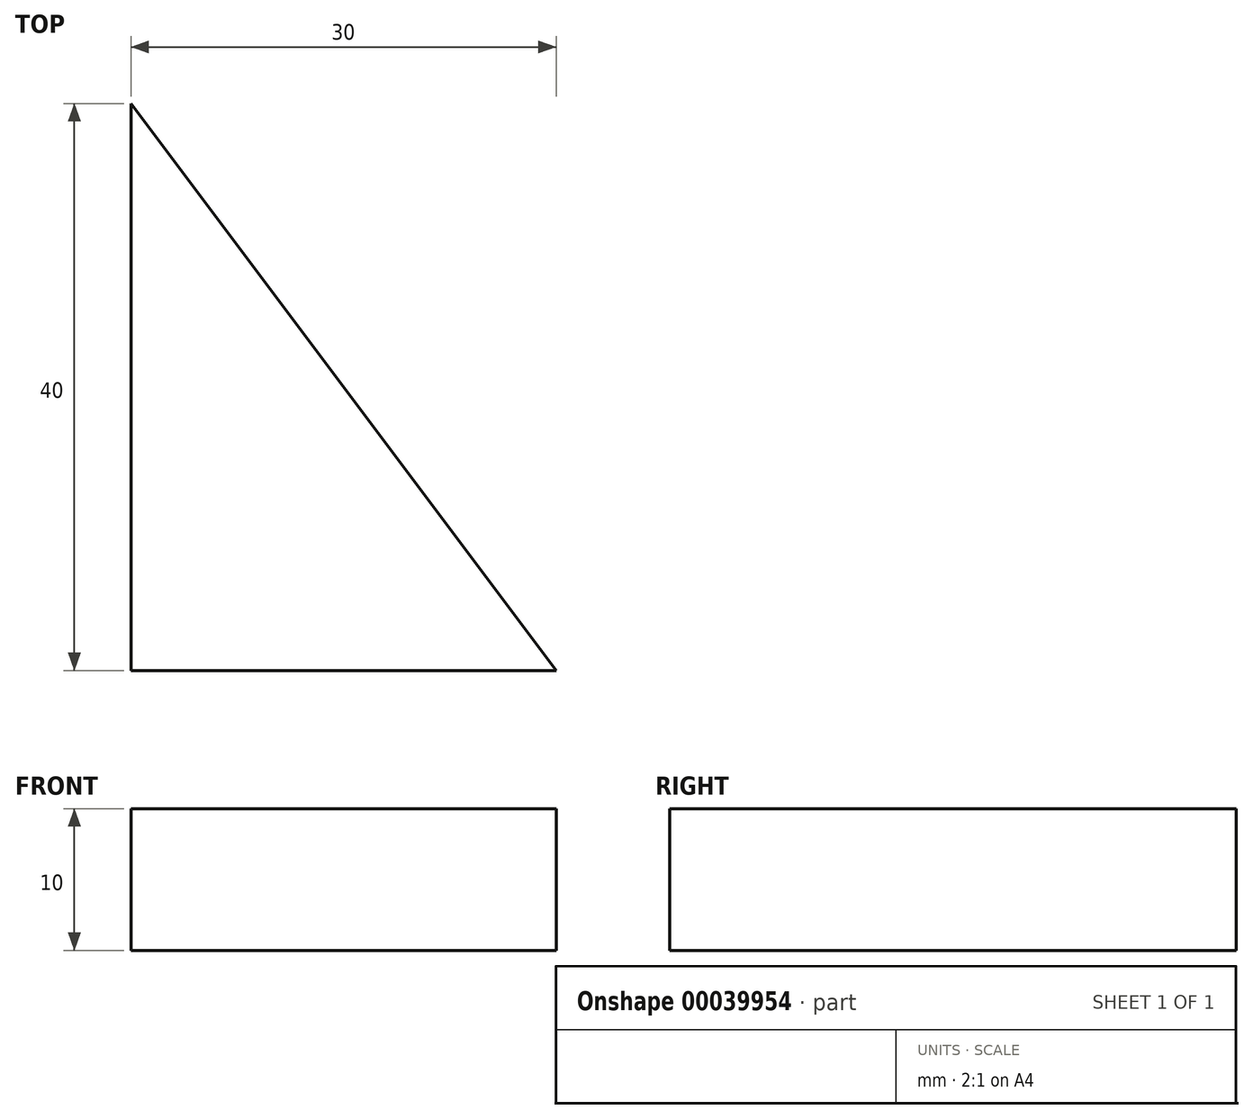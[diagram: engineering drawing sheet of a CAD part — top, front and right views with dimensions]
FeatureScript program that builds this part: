
annotation { "Feature Type Name" : "Feature", "Feature Type Description" : "" }
export const myFeature = defineFeature(function(context is Context, id is Id, definition is map)
    precondition{}
    {
        {
            var Q0;
            Q0=qCreatedBy(makeId("Top.planeOp"),FACE);
            var sketch = newSketch(context, id + "F0", { "sketchPlane" : qUnion([Q0])});
            skLineSegment(sketch, "E0", {"start": v(18.58, 70) * mm, "end": v(18.58, 30) * mm});
            skLineSegment(sketch, "E1", {"start": v(18.58, 70) * mm, "end": v(48.58, 30) * mm});
            skLineSegment(sketch, "E2", {"start": v(18.58, 30) * mm, "end": v(48.58, 30) * mm});
            skLineSegment(sketch, "E3.bottom", {"start": v(18.58, 30) * mm, "end": v(48.3, 30) * mm});
            skLineSegment(sketch, "E3.top", {"start": v(18.58, 0) * mm, "end": v(48.3, 0) * mm});
            skLineSegment(sketch, "E3.left", {"start": v(18.58, 30) * mm, "end": v(18.58, 0) * mm});
            skLineSegment(sketch, "E3.right", {"start": v(48.3, 30) * mm, "end": v(48.3, 0) * mm});
            skSolve(sketch);
        }
        {
            var Q0;
            Q0=makeQuery(id+"F0.imprint","IMPRINT",FACE,{"disambiguationData":[TD([[makeQuery(id+"F0.imprint","IMPRINT",EDGE,{"derivedFrom":sQuery(id+"F0.wireOp",EDGE,"E0")}),1.0]])]});
            var Q1;
            Q1=makeQuery(id+"F0.imprint","IMPRINT",FACE,{"disambiguationData":[TD([[makeQuery(id+"F0.imprint","IMPRINT",EDGE,{"derivedFrom":sQuery(id+"F0.wireOp",EDGE,"E3.bottom")}),-1.0]])]});
            extrude(context, id + "F1", {"entities" : qUnion([Q0, Q1]), "depth" : 10 * mm});
        }
    });
